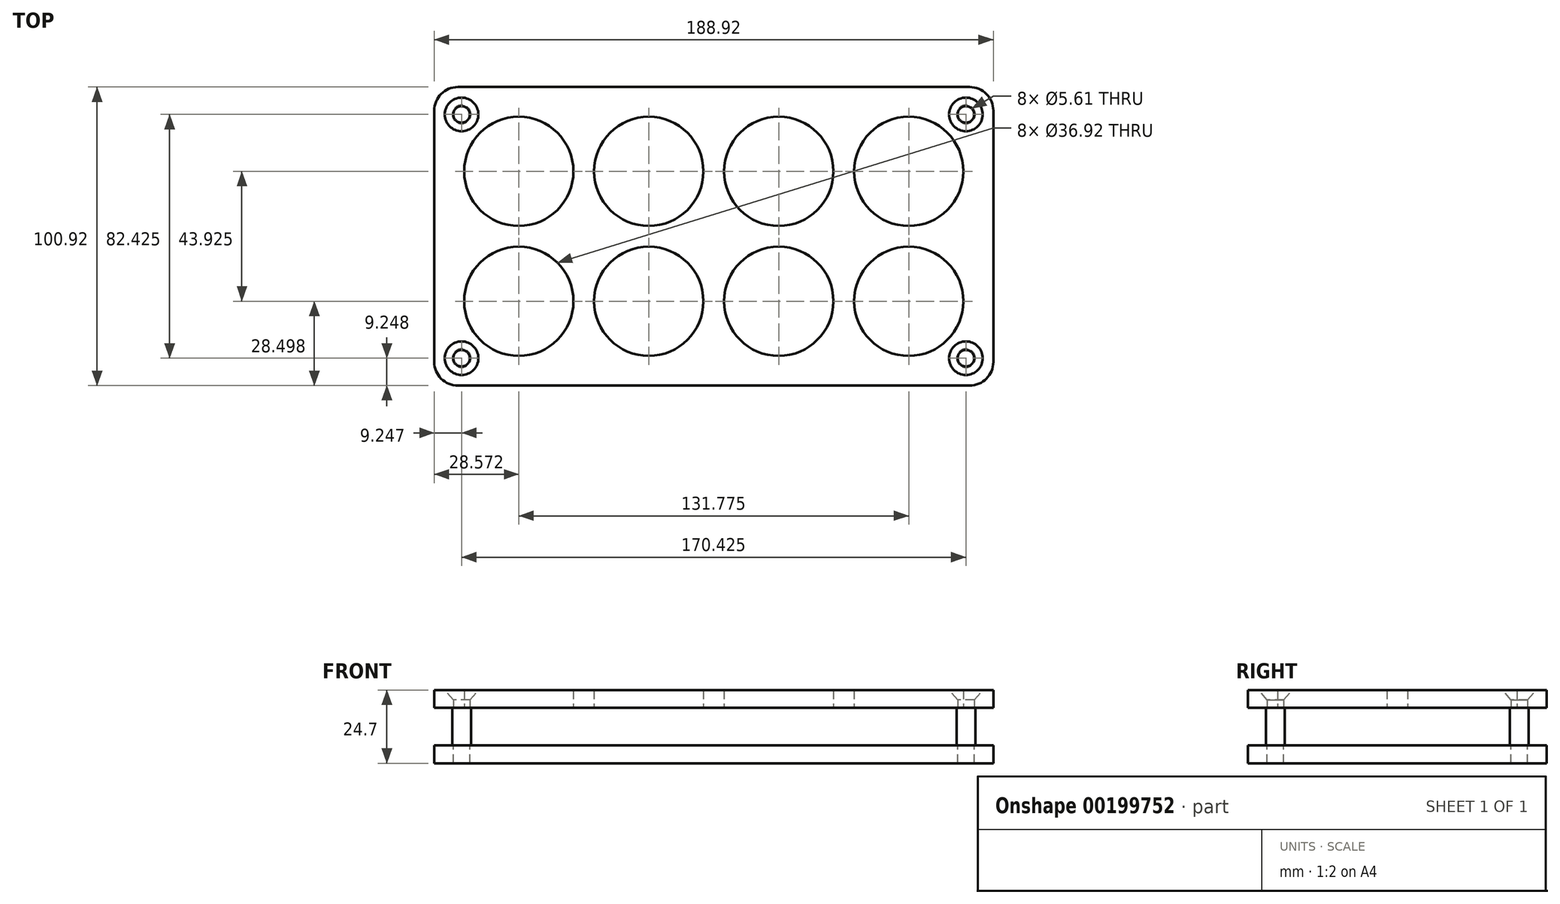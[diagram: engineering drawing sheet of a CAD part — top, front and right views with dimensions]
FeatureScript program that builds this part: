
annotation { "Feature Type Name" : "Feature", "Feature Type Description" : "" }
export const myFeature = defineFeature(function(context is Context, id is Id, definition is map)
    precondition{}
    {
        {
            var Q0;
            Q0=qCreatedBy(makeId("Top.planeOp"),FACE);
            var sketch = newSketch(context, id + "F0", { "sketchPlane" : qUnion([Q0])});
            skLineSegment(sketch, "E0.bottom", {"start": v(86.46, -50.46) * mm, "end": v(-86.46, -50.46) * mm});
            skLineSegment(sketch, "E0.top", {"start": v(86.46, 50.46) * mm, "end": v(-86.46, 50.46) * mm});
            skLineSegment(sketch, "E0.left", {"start": v(94.46, -42.46) * mm, "end": v(94.46, 42.46) * mm});
            skLineSegment(sketch, "E0.right", {"start": v(-94.46, -42.46) * mm, "end": v(-94.46, 42.46) * mm});
            skPoint(sketch, "E0.middle", {"position": v(0, 0) * mm});
            skPoint(sketch, "E1.visualSharp", {"position": v(-94.46, 50.46) * mm});
            skArc(sketch, "E1.filletArc", {"start": v(-86.46, 50.46) * mm, "mid": v(-92.12, 48.12) * mm, "end": v(-94.46, 42.46) * mm});
            skPoint(sketch, "E2.visualSharp", {"position": v(-94.46, -50.46) * mm});
            skArc(sketch, "E2.filletArc", {"start": v(-94.46, -42.46) * mm, "mid": v(-92.12, -48.12) * mm, "end": v(-86.46, -50.46) * mm});
            skPoint(sketch, "E3.visualSharp", {"position": v(94.46, -50.46) * mm});
            skArc(sketch, "E3.filletArc", {"start": v(86.46, -50.46) * mm, "mid": v(92.12, -48.12) * mm, "end": v(94.46, -42.46) * mm});
            skPoint(sketch, "E4.visualSharp", {"position": v(94.46, 50.46) * mm});
            skArc(sketch, "E4.filletArc", {"start": v(94.46, 42.46) * mm, "mid": v(92.12, 48.12) * mm, "end": v(86.46, 50.46) * mm});
            skSolve(sketch);
        }
        {
            var Q0;
            Q0=makeQuery(id+"F0.imprint","IMPRINT",FACE,{"disambiguationData":[TD([[makeQuery(id+"F0.imprint","IMPRINT",EDGE,{"derivedFrom":sQuery(id+"F0.wireOp",EDGE,"E0.bottom")}),-1.0]])]});
            extrude(context, id + "F1", {"entities" : qUnion([Q0]), "depth" : 6 * mm});
        }
        {
            var Q0;
            Q0=makeQuery(id+"F1.opExtrude","CAP_FACE",FACE,{"disambiguationData":[OSD([sQuery(id+"F0.wireOp",EDGE,"E0.bottom"),sQuery(id+"F0.wireOp",EDGE,"E0.top"),sQuery(id+"F0.wireOp",EDGE,"E0.left"),sQuery(id+"F0.wireOp",EDGE,"E0.right"),sQuery(id+"F0.wireOp",EDGE,"E1.filletArc"),sQuery(id+"F0.wireOp",EDGE,"E2.filletArc"),sQuery(id+"F0.wireOp",EDGE,"E3.filletArc"),sQuery(id+"F0.wireOp",EDGE,"E4.filletArc")])],"isStart":false});
            var sketch = newSketch(context, id + "F2", { "sketchPlane" : qUnion([Q0])});
            skLineSegment(sketch, "E5", {"start": v(-117.06, 41.21) * mm, "end": v(125.07, 41.21) * mm, "construction": true});
            skLineSegment(sketch, "E6", {"start": v(85.21, 60.19) * mm, "end": v(85.21, -59.59) * mm, "construction": true});
            skLineSegment(sketch, "E7", {"start": v(-85.21, 60.19) * mm, "end": v(-85.21, -59.59) * mm, "construction": true});
            skLineSegment(sketch, "E8", {"start": v(-117.06, -41.21) * mm, "end": v(125.07, -41.21) * mm, "construction": true});
            skCircle(sketch, "E9", {"center": v(-85.21, 41.21) * mm, "radius": 2.8 * mm});
            skCircle(sketch, "E10", {"center": v(-85.21, -41.21) * mm, "radius": 2.8 * mm});
            skCircle(sketch, "E11", {"center": v(85.21, -41.21) * mm, "radius": 2.8 * mm});
            skCircle(sketch, "E12", {"center": v(85.21, 41.21) * mm, "radius": 2.8 * mm});
            skSolve(sketch);
        }
        {
            var Q0;
            Q0=makeQuery(id+"F2.imprint","IMPRINT",FACE,{"disambiguationData":[TD([[makeQuery(id+"F2.imprint","IMPRINT",EDGE,{"derivedFrom":sQuery(id+"F2.wireOp",EDGE,"E9")}),1.0]])]});
            var Q1;
            Q1=makeQuery(id+"F2.imprint","IMPRINT",FACE,{"disambiguationData":[TD([[makeQuery(id+"F2.imprint","IMPRINT",EDGE,{"derivedFrom":sQuery(id+"F2.wireOp",EDGE,"E11")}),1.0]])]});
            var Q2;
            Q2=makeQuery(id+"F2.imprint","IMPRINT",FACE,{"disambiguationData":[TD([[makeQuery(id+"F2.imprint","IMPRINT",EDGE,{"derivedFrom":sQuery(id+"F2.wireOp",EDGE,"E10")}),1.0]])]});
            var Q3;
            Q3=makeQuery(id+"F2.imprint","IMPRINT",FACE,{"disambiguationData":[TD([[makeQuery(id+"F2.imprint","IMPRINT",EDGE,{"derivedFrom":sQuery(id+"F2.wireOp",EDGE,"E12")}),1.0]])]});
            extrude(context, id + "F3", {"entities" : qUnion([Q0, Q1, Q2, Q3]), "operationType" : NewBodyOperationType.REMOVE, "endBound" : BoundingType.UP_TO_NEXT, "oppositeDirection" : true, "depth" : 25 * mm});
        }
        {
            var Q0;
            Q0=makeQuery(id+"F1.opExtrude","CAP_FACE",FACE,{"disambiguationData":[OSD([sQuery(id+"F0.wireOp",EDGE,"E0.bottom"),sQuery(id+"F0.wireOp",EDGE,"E0.top"),sQuery(id+"F0.wireOp",EDGE,"E0.left"),sQuery(id+"F0.wireOp",EDGE,"E0.right"),sQuery(id+"F0.wireOp",EDGE,"E1.filletArc"),sQuery(id+"F0.wireOp",EDGE,"E2.filletArc"),sQuery(id+"F0.wireOp",EDGE,"E3.filletArc"),sQuery(id+"F0.wireOp",EDGE,"E4.filletArc")])],"isStart":false});
            cPlane(context, id + "F4", {"entities" : qUnion([Q0]), "cplaneType" : CPlaneType.OFFSET, "offset" : 12.7 * mm, "width" : 150 * mm, "height" : 150 * mm});
        }
        {
            var Q0;
            Q0=makeQuery(id+"F1.opExtrude","CAP_FACE",FACE,{"disambiguationData":[OSD([sQuery(id+"F0.wireOp",EDGE,"E0.bottom"),sQuery(id+"F0.wireOp",EDGE,"E0.top"),sQuery(id+"F0.wireOp",EDGE,"E0.left"),sQuery(id+"F0.wireOp",EDGE,"E0.right"),sQuery(id+"F0.wireOp",EDGE,"E1.filletArc"),sQuery(id+"F0.wireOp",EDGE,"E2.filletArc"),sQuery(id+"F0.wireOp",EDGE,"E3.filletArc"),sQuery(id+"F0.wireOp",EDGE,"E4.filletArc")])],"isStart":false});
            cPlane(context, id + "F5", {"entities" : qUnion([Q0]), "cplaneType" : CPlaneType.OFFSET, "offset" : 0 * mm, "width" : 150 * mm, "height" : 150 * mm});
        }
        {
            var Q0;
            Q0=qCreatedBy(id+"F5.planeOp",FACE);
            var sketch = newSketch(context, id + "F6", { "sketchPlane" : qUnion([Q0])});
            skCircle(sketch, "E13", {"center": v(-85.21, 41.21) * mm, "radius": 3.18 * mm});
            skCircle(sketch, "E14", {"center": v(85.21, 41.21) * mm, "radius": 3.18 * mm});
            skCircle(sketch, "E15", {"center": v(85.21, -41.21) * mm, "radius": 3.18 * mm});
            skCircle(sketch, "E16", {"center": v(-85.21, -41.21) * mm, "radius": 3.18 * mm});
            skSolve(sketch);
        }
        {
            var Q0;
            Q0 = qSketchRegion(id + "F6", true);
            var Q1;
            Q1=sQuery(id+"F6.wireOp",EDGE,"E13");
            var Q2;
            Q2=sQuery(id+"F6.wireOp",EDGE,"E14");
            var Q3;
            Q3=sQuery(id+"F6.wireOp",EDGE,"E15");
            var Q4;
            Q4=sQuery(id+"F6.wireOp",EDGE,"E16");
            extrude(context, id + "F7", {"entities" : qUnion([Q0]), "surfaceEntities" : qUnion([Q1, Q2, Q3, Q4]), "depth" : 12.7 * mm});
        }
        {
            var Q0;
            Q0=qCreatedBy(id+"F4.planeOp",FACE);
            var sketch = newSketch(context, id + "F8", { "sketchPlane" : qUnion([Q0])});
            skArc(sketch, "E17.0", {"start": v(-86.46, 50.46) * mm, "mid": v(-92.12, 48.12) * mm, "end": v(-94.46, 42.46) * mm});
            skLineSegment(sketch, "E18.0", {"start": v(86.46, 50.46) * mm, "end": v(-86.46, 50.46) * mm});
            skArc(sketch, "E19.0", {"start": v(94.46, 42.46) * mm, "mid": v(92.12, 48.12) * mm, "end": v(86.46, 50.46) * mm});
            skLineSegment(sketch, "E20.0", {"start": v(94.46, -42.46) * mm, "end": v(94.46, 42.46) * mm});
            skArc(sketch, "E21.0", {"start": v(86.46, -50.46) * mm, "mid": v(92.12, -48.12) * mm, "end": v(94.46, -42.46) * mm});
            skLineSegment(sketch, "E22.0", {"start": v(86.46, -50.46) * mm, "end": v(-86.46, -50.46) * mm});
            skArc(sketch, "E23.0", {"start": v(-94.46, -42.46) * mm, "mid": v(-92.12, -48.12) * mm, "end": v(-86.46, -50.46) * mm});
            skLineSegment(sketch, "E24.0", {"start": v(-94.46, -42.46) * mm, "end": v(-94.46, 42.46) * mm});
            skCircle(sketch, "E25.0", {"center": v(-85.21, 41.21) * mm, "radius": 2.8 * mm});
            skCircle(sketch, "E26.0", {"center": v(85.21, 41.21) * mm, "radius": 2.8 * mm});
            skCircle(sketch, "E27.0", {"center": v(85.21, -41.21) * mm, "radius": 2.8 * mm});
            skCircle(sketch, "E28.0", {"center": v(-85.21, -41.21) * mm, "radius": 2.8 * mm});
            skCircle(sketch, "E29", {"center": v(-65.89, 21.96) * mm, "radius": 18.46 * mm});
            skCircle(sketch, "E30.0.1.0", {"center": v(-65.89, -21.96) * mm, "radius": 18.46 * mm});
            skCircle(sketch, "E30.1.0.0", {"center": v(-21.96, 21.96) * mm, "radius": 18.46 * mm});
            skCircle(sketch, "E30.1.1.0", {"center": v(-21.96, -21.96) * mm, "radius": 18.46 * mm});
            skCircle(sketch, "E30.2.0.0", {"center": v(21.96, 21.96) * mm, "radius": 18.46 * mm});
            skCircle(sketch, "E30.2.1.0", {"center": v(21.96, -21.96) * mm, "radius": 18.46 * mm});
            skCircle(sketch, "E30.3.0.0", {"center": v(65.89, 21.96) * mm, "radius": 18.46 * mm});
            skCircle(sketch, "E30.3.1.0", {"center": v(65.89, -21.96) * mm, "radius": 18.46 * mm});
            skLineSegment(sketch, "E30.direction1", {"start": v(-65.89, 21.96) * mm, "end": v(-21.96, 21.96) * mm, "construction": true});
            skLineSegment(sketch, "E30.direction2", {"start": v(-65.89, 21.96) * mm, "end": v(-65.89, -21.96) * mm, "construction": true});
            skPoint(sketch, "E31", {"position": v(-84.35, -21.96) * mm});
            skPoint(sketch, "E32", {"position": v(-65.89, -40.43) * mm});
            skPoint(sketch, "E33", {"position": v(-65.89, 40.42) * mm});
            skPoint(sketch, "E34", {"position": v(84.35, -21.96) * mm});
            skLineSegment(sketch, "E35", {"start": v(-84.35, -21.96) * mm, "end": v(-94.46, -21.96) * mm, "construction": true});
            skLineSegment(sketch, "E36", {"start": v(84.35, -21.96) * mm, "end": v(94.46, -21.96) * mm, "construction": true});
            skSolve(sketch);
        }
        {
            var Q0;
            Q0=makeQuery(id+"F8.imprint","IMPRINT",FACE,{"disambiguationData":[TD([[makeQuery(id+"F8.imprint","IMPRINT",EDGE,{"derivedFrom":sQuery(id+"F8.wireOp",EDGE,"E17.0")}),1.0]])]});
            extrude(context, id + "F9", {"entities" : qUnion([Q0]), "depth" : 6 * mm});
        }
        {
            var Q0;
            Q0=makeQuery(id+"F9.opExtrude","CAP_EDGE",EDGE,{"disambiguationData":[OSD([sQuery(id+"F8.wireOp",EDGE,"E28.0")])],"isStart":false});
            var Q1;
            Q1=makeQuery(id+"F9.opExtrude","CAP_EDGE",EDGE,{"disambiguationData":[OSD([sQuery(id+"F8.wireOp",EDGE,"E25.0")])],"isStart":false});
            var Q2;
            Q2=makeQuery(id+"F9.opExtrude","CAP_EDGE",EDGE,{"disambiguationData":[OSD([sQuery(id+"F8.wireOp",EDGE,"E26.0")])],"isStart":false});
            var Q3;
            Q3=makeQuery(id+"F9.opExtrude","CAP_EDGE",EDGE,{"disambiguationData":[OSD([sQuery(id+"F8.wireOp",EDGE,"E27.0")])],"isStart":false});
            var Q4;
            Q4=makeQuery(id+"F3.boolean.opBoolean","COPY",EDGE,{"derivedFrom":makeQuery(id+"F3.opExtrude","TWEAK_EDGE",EDGE,{"derivedFrom":[makeQuery(id+"F1.opExtrude","CAP_FACE",FACE,{"disambiguationData":[OSD([sQuery(id+"F0.wireOp",EDGE,"E0.bottom"),sQuery(id+"F0.wireOp",EDGE,"E0.top"),sQuery(id+"F0.wireOp",EDGE,"E0.left"),sQuery(id+"F0.wireOp",EDGE,"E0.right"),sQuery(id+"F0.wireOp",EDGE,"E1.filletArc"),sQuery(id+"F0.wireOp",EDGE,"E2.filletArc"),sQuery(id+"F0.wireOp",EDGE,"E3.filletArc"),sQuery(id+"F0.wireOp",EDGE,"E4.filletArc")])],"isStart":true}),makeQuery(id+"F2.imprint","IMPRINT",EDGE,{"derivedFrom":sQuery(id+"F2.wireOp",EDGE,"E11")})]})});
            var Q5;
            Q5=makeQuery(id+"F3.boolean.opBoolean","COPY",EDGE,{"derivedFrom":makeQuery(id+"F3.opExtrude","TWEAK_EDGE",EDGE,{"derivedFrom":[makeQuery(id+"F1.opExtrude","CAP_FACE",FACE,{"disambiguationData":[OSD([sQuery(id+"F0.wireOp",EDGE,"E0.bottom"),sQuery(id+"F0.wireOp",EDGE,"E0.top"),sQuery(id+"F0.wireOp",EDGE,"E0.left"),sQuery(id+"F0.wireOp",EDGE,"E0.right"),sQuery(id+"F0.wireOp",EDGE,"E1.filletArc"),sQuery(id+"F0.wireOp",EDGE,"E2.filletArc"),sQuery(id+"F0.wireOp",EDGE,"E3.filletArc"),sQuery(id+"F0.wireOp",EDGE,"E4.filletArc")])],"isStart":true}),makeQuery(id+"F2.imprint","IMPRINT",EDGE,{"derivedFrom":sQuery(id+"F2.wireOp",EDGE,"E12")})]})});
            var Q6;
            Q6=makeQuery(id+"F3.boolean.opBoolean","COPY",EDGE,{"derivedFrom":makeQuery(id+"F3.opExtrude","TWEAK_EDGE",EDGE,{"derivedFrom":[makeQuery(id+"F1.opExtrude","CAP_FACE",FACE,{"disambiguationData":[OSD([sQuery(id+"F0.wireOp",EDGE,"E0.bottom"),sQuery(id+"F0.wireOp",EDGE,"E0.top"),sQuery(id+"F0.wireOp",EDGE,"E0.left"),sQuery(id+"F0.wireOp",EDGE,"E0.right"),sQuery(id+"F0.wireOp",EDGE,"E1.filletArc"),sQuery(id+"F0.wireOp",EDGE,"E2.filletArc"),sQuery(id+"F0.wireOp",EDGE,"E3.filletArc"),sQuery(id+"F0.wireOp",EDGE,"E4.filletArc")])],"isStart":true}),makeQuery(id+"F2.imprint","IMPRINT",EDGE,{"derivedFrom":sQuery(id+"F2.wireOp",EDGE,"E10")})]})});
            var Q7;
            Q7=makeQuery(id+"F3.boolean.opBoolean","COPY",EDGE,{"derivedFrom":makeQuery(id+"F3.opExtrude","TWEAK_EDGE",EDGE,{"derivedFrom":[makeQuery(id+"F1.opExtrude","CAP_FACE",FACE,{"disambiguationData":[OSD([sQuery(id+"F0.wireOp",EDGE,"E0.bottom"),sQuery(id+"F0.wireOp",EDGE,"E0.top"),sQuery(id+"F0.wireOp",EDGE,"E0.left"),sQuery(id+"F0.wireOp",EDGE,"E0.right"),sQuery(id+"F0.wireOp",EDGE,"E1.filletArc"),sQuery(id+"F0.wireOp",EDGE,"E2.filletArc"),sQuery(id+"F0.wireOp",EDGE,"E3.filletArc"),sQuery(id+"F0.wireOp",EDGE,"E4.filletArc")])],"isStart":true}),makeQuery(id+"F2.imprint","IMPRINT",EDGE,{"derivedFrom":sQuery(id+"F2.wireOp",EDGE,"E9")})]})});
            chamfer(context, id + "F10", {"entities" : qUnion([Q0, Q1, Q2, Q3, Q4, Q5, Q6, Q7]), "chamferType" : ChamferType.OFFSET_ANGLE, "width" : 3.3 * mm, "oppositeDirection" : false, "angle" : 82 / 2 * degree, "tangentPropagation" : true});
        }
    });
